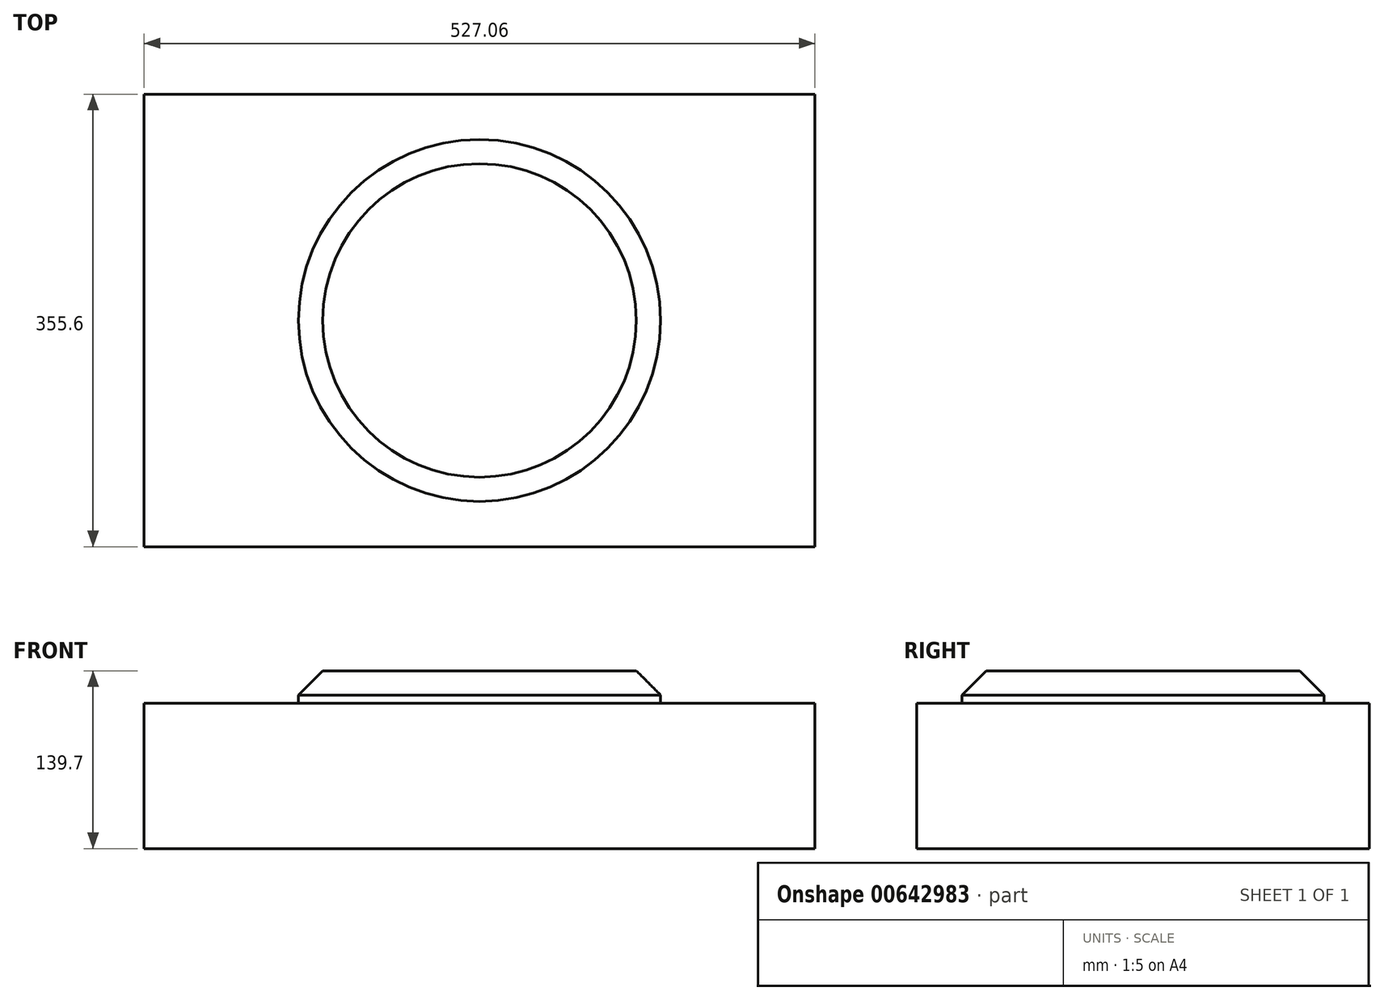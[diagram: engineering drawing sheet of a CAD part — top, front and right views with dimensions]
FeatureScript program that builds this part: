
annotation { "Feature Type Name" : "Feature", "Feature Type Description" : "" }
export const myFeature = defineFeature(function(context is Context, id is Id, definition is map)
    precondition{}
    {
        {
            var Q0;
            Q0=qCreatedBy(makeId("Top.planeOp"),FACE);
            var sketch = newSketch(context, id + "F0", { "sketchPlane" : qUnion([Q0])});
            skPoint(sketch, "E0.middle", {"position": v(0, 0) * mm});
            skLineSegment(sketch, "E1.bottom", {"start": v(263.53, 177.8) * mm, "end": v(-263.53, 177.8) * mm});
            skLineSegment(sketch, "E1.top", {"start": v(263.53, -177.8) * mm, "end": v(-263.53, -177.8) * mm});
            skLineSegment(sketch, "E1.left", {"start": v(263.53, 177.8) * mm, "end": v(263.53, -177.8) * mm});
            skLineSegment(sketch, "E1.right", {"start": v(-263.53, 177.8) * mm, "end": v(-263.53, -177.8) * mm});
            skSolve(sketch);
        }
        {
            var Q0;
            Q0=qSketchRegion(id+"F0",true);
            extrude(context, id + "F1", {"entities" : qUnion([Q0]), "depth" : 114.3 * mm});
        }
        {
            var Q0;
            Q0=qCreatedBy(makeId("Right.planeOp"),FACE);
            var sketch = newSketch(context, id + "F2", { "sketchPlane" : qUnion([Q0])});
            skLineSegment(sketch, "E2.0", {"start": v(-142.24, 114.3) * mm, "end": v(0, 114.3) * mm});
            skLineSegment(sketch, "E3", {"start": v(0, 139.7) * mm, "end": v(-123.19, 139.7) * mm});
            skLineSegment(sketch, "E4", {"start": v(0, 139.7) * mm, "end": v(0, 114.3) * mm});
            skLineSegment(sketch, "E5", {"start": v(-123.19, 139.7) * mm, "end": v(-142.24, 120.65) * mm});
            skLineSegment(sketch, "E6", {"start": v(-142.24, 114.3) * mm, "end": v(-142.24, 120.65) * mm});
            skSolve(sketch);
        }
        {
            var Q0;
            Q0=qSketchRegion(id+"F2",true);
            var Q1;
            Q1=sQuery(id+"F2.wireOp",EDGE,"E4");
            revolve(context, id + "F3", {"operationType" : NewBodyOperationType.ADD, "entities" : qUnion([Q0]), "axis" : qUnion([Q1]), "revolveType" : RevolveType.FULL});
        }
    });
